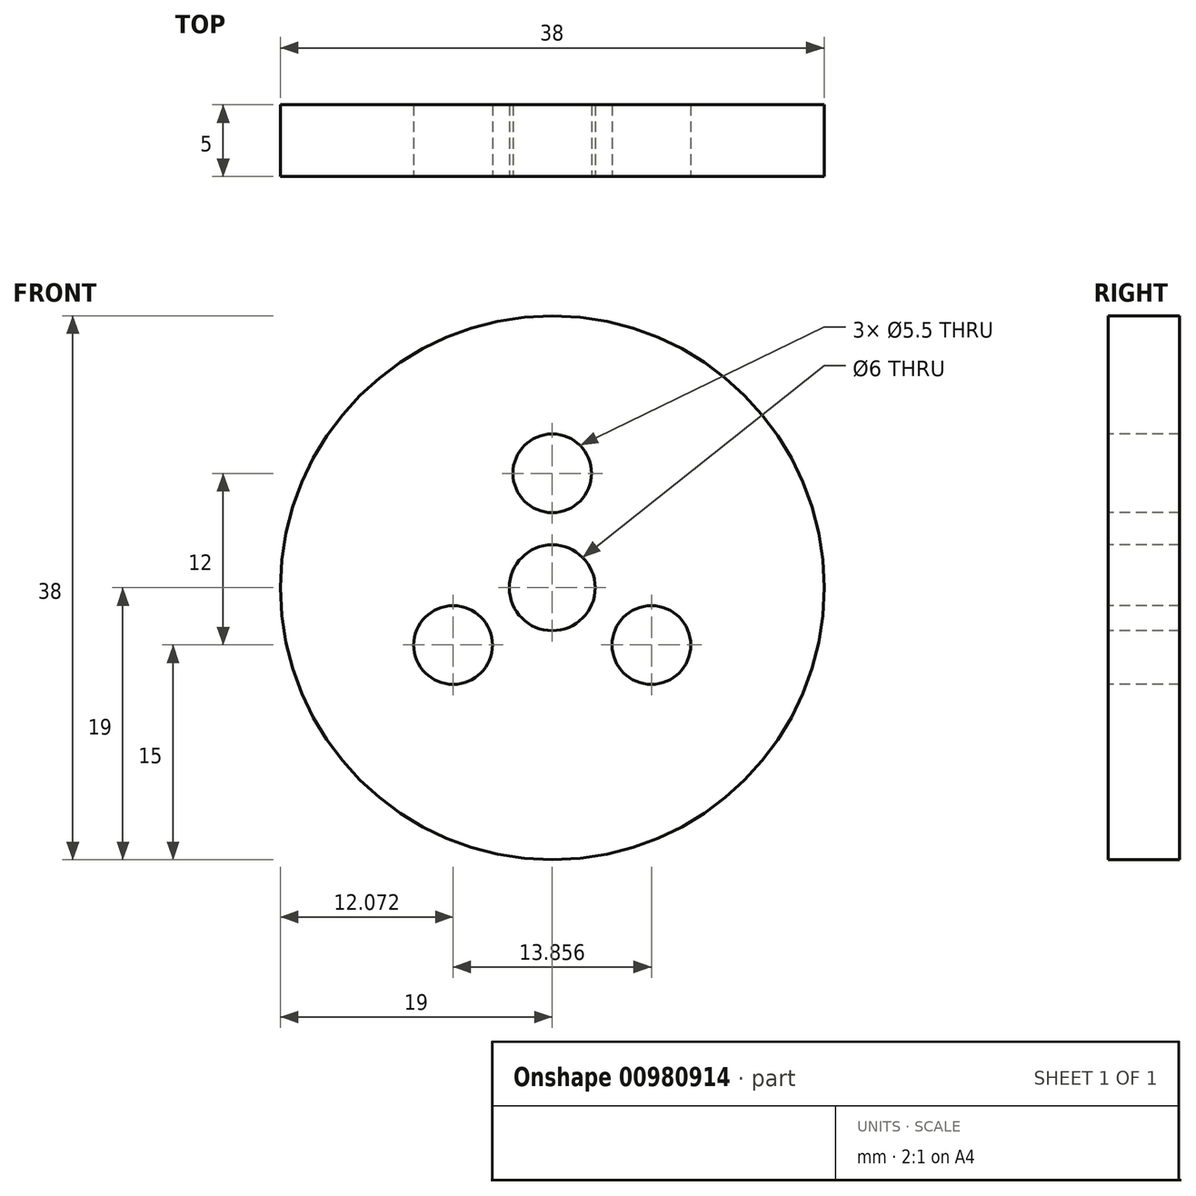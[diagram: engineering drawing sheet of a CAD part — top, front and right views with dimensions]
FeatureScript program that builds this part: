
annotation { "Feature Type Name" : "Feature", "Feature Type Description" : "" }
export const myFeature = defineFeature(function(context is Context, id is Id, definition is map)
    precondition{}
    {
        {
            var Q0;
            Q0=qCreatedBy(makeId("Front.planeOp"),FACE);
            var sketch = newSketch(context, id + "F0", { "sketchPlane" : qUnion([Q0])});
            skCircle(sketch, "E0", {"center": v(0, 0) * mm, "radius": 19 * mm});
            skSolve(sketch);
        }
        {
            var Q0;
            Q0 = qSketchRegion(id + "F0", true);
            extrude(context, id + "F1", {"entities" : qUnion([Q0]), "depth" : 5 * mm, "offsetDistance" : 25 * mm});
        }
        {
            var Q0;
            Q0=makeQuery(id+"F1.opExtrude","CAP_FACE",FACE,{"disambiguationData":[OSD([sQuery(id+"F0.wireOp",EDGE,"E0")])],"isStart":false});
            var sketch = newSketch(context, id + "F2", { "sketchPlane" : qUnion([Q0])});
            skCircle(sketch, "E1", {"center": v(0, 0) * mm, "radius": 11.5 * mm});
            skSolve(sketch);
        }
        {
            var Q0;
            Q0=makeQuery(id+"F1.opExtrude","CAP_FACE",FACE,{"disambiguationData":[OSD([sQuery(id+"F0.wireOp",EDGE,"E0")])],"isStart":false});
            var sketch = newSketch(context, id + "F3", { "sketchPlane" : qUnion([Q0])});
            skPoint(sketch, "E2", {"position": v(-6.93, -4) * mm});
            skPoint(sketch, "E3.1.0", {"position": v(6.93, -4) * mm});
            skPoint(sketch, "E3.center", {"position": v(0, 0) * mm});
            skPoint(sketch, "E4.0.2.0", {"position": v(0, 8) * mm});
            skSolve(sketch);
        }
        {
            var Q0;
            Q0=sQuery(id+"F3.wireOp",VERTEX,"E2");
            var Q1;
            Q1=sQuery(id+"F3.wireOp",VERTEX,"cb4aecf5-d41c-4924-82a2-1884036406db");
            var Q2;
            Q2=sQuery(id+"F3.wireOp",VERTEX,"E4.0.2.0");
            var Q3;
            Q3=sQuery(id+"F3.wireOp",VERTEX,"E3.1.0");
            var Q4;
            Q4=makeQuery(id+"F1.opExtrude","SWEPT_BODY",BODY,{"disambiguationData":[OSD([sQuery(id+"F0.wireOp",EDGE,"E0")])]});
            hole(context, id + "F4", {"style" : HoleStyle.SIMPLE, "endStyle" : HoleEndStyle.THROUGH, "standardTappedOrClearance" : lookupTablePath({ "standard" : "ISO", "size" : "5.5", "type" : "Drilled" }), "standardBlindInLast" : lookupTablePath({ "standard" : "ISO", "size" : "5.5", "type" : "Drilled" }), "holeDiameter" : 5.5 * mm, "majorDiameter" : 20 * mm, "isTappedThrough" : true, "tappedDepth" : 7.6 * mm, "tapClearance" : 3, "startFromSketch" : true, "locations" : qUnion([Q0, Q1, Q2, Q3]), "scope" : qUnion([Q4])});
        }
        {
            var Q0;
            Q0=makeQuery(id+"F2.imprint","IMPRINT",FACE,{"disambiguationData":[TD([[makeQuery(id+"F2.imprint","IMPRINT",EDGE,{"derivedFrom":sQuery(id+"F2.wireOp",EDGE,"E1")}),1.0]])]});
            var sketch = newSketch(context, id + "F5", { "sketchPlane" : qUnion([Q0])});
            skPoint(sketch, "E5", {"position": v(0, 0) * mm});
            skSolve(sketch);
        }
        {
            var Q0;
            Q0=sQuery(id+"F5.wireOp",VERTEX,"E5");
            var Q1;
            Q1=makeQuery(id+"F1.opExtrude","SWEPT_BODY",BODY,{"disambiguationData":[OSD([sQuery(id+"F0.wireOp",EDGE,"E0")])]});
            hole(context, id + "F6", {"style" : HoleStyle.SIMPLE, "endStyle" : HoleEndStyle.THROUGH, "standardTappedOrClearance" : lookupTablePath({ "standard" : "ISO", "size" : "6", "type" : "Drilled" }), "standardBlindInLast" : lookupTablePath({ "standard" : "ISO", "size" : "6", "type" : "Drilled" }), "holeDiameter" : 6 * mm, "majorDiameter" : 5 * mm, "isTappedThrough" : true, "tappedDepth" : 7.6 * mm, "tapClearance" : 3, "startFromSketch" : true, "locations" : qUnion([Q0]), "scope" : qUnion([Q1])});
        }
    });
